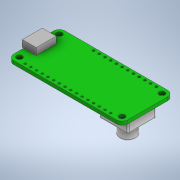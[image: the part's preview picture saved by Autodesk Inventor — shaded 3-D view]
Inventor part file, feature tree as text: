
AUTODESK INVENTOR PART (.ipt)
format: ipt  version: 2021 (Build 250183000, 183)  size: 244,736 bytes
history: native  units: in
note: dims shown in document units (in); Inventor stores cm internally (conversion verified against a paired STEP export)
features: extrude x7, sketch x7, pattern_linear x2, fillet x1, projected_geometry x1
ambient origin geometry x8: Origin, YZ Plane, XZ Plane, XY Plane, X Axis, Y Axis, Z Axis, Center Point
bodies: Solid1 (feature_tree)
feature tree (18):
  extrude  "Extrusion1"  Depth=0.9in
  extrude  "Extrusion4"  Depth=0.7in
  extrude  "Extrusion6"  Depth=0.1in
  pattern_linear  "Rectangular Pattern1"  Spacing1=0.063in  [1 undecoded]
  extrude  "Extrusion7"  Depth=0.025in
  pattern_linear  "Rectangular Pattern2"  Spacing1=0.245in  [1 undecoded]
  extrude  "Extrusion8"  Depth=0.1181in TaperAngle=0.0deg
  extrude  "Extrusion9"  Depth=0.1181in
  fillet  "Fillet2"  Radius=0.05in
  extrude  "Extrusion10"  Depth=0.05in
  sketch  "Sketch1"  dims[d0=2.0in d1=0.9in]
  sketch  "Sketch4"  dims[d2=0.1in d6=0.7in]
  sketch  "Sketch6"  dims[d9=0.35in d10=0.1in]
  sketch  "Sketch7"  dims[d11=0.1in]
  sketch  "Sketch8"  dims[d13=0.1in]
  sketch  "Sketch9"  dims[d14=0.1in]
  sketch  "Sketch10"  dims[d15=0.1in d16=0.063in d17=0.0in d34=0.025in d35=0.245in d38=0.1181in d39=0.0in d46=0.0394in d47=0.05in d48=0.05in d49=0.0in d50=0.0in d51=6.2992in d53=0.1in d54=1.15in d55=0.05in d56=0.0394in d57=0.0in d58=0.0in d59=4.7244in d61=0.1in d62=0.35in d63=0.5in d64=1.65in d65=0.2638in d66=0.0in d67=0.28in d69=0.25in d70=0.0in d71=0.025in d72=0.32in d74=0.525in d75=0.1181in d76=0.0in]
  projected_geometry  "Project Cut Edges1"
note: 2 required parameter values undecoded (feature->parameter linkage not recoverable at this tier; creation-order binding heuristic only, values carry confidence <= 0.55)
